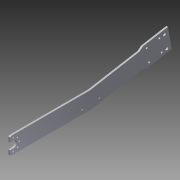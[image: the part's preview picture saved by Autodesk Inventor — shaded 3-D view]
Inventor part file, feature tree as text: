
AUTODESK INVENTOR PART (.ipt)
format: ipt  version: 2013 (Build 170138000, 138)  size: 186,368 bytes
history: native  units: mm
features: sketch x6, hole x5, other x2, extrude x2, pattern_circular x1
ambient origin geometry x8: Origin, YZ Plane, XZ Plane, XY Plane, X Axis, Y Axis, Z Axis, Center Point
feature tree (16):
  other  "ソリッド1"
  extrude  "押し出し1"  Depth=20.0mm
  hole  "穴2"  [1 undecoded]
  extrude  "押し出し2"  Depth=10.0mm
  hole  "穴3"  [1 undecoded]
  hole  "穴4"  [1 undecoded]
  pattern_circular  "円形状パターン3"  [2 undecoded]
  hole  "穴5"  [1 undecoded]
  hole  "穴6"  [1 undecoded]
  sketch  "スケッチ4"
  sketch  "スケッチ5"
  sketch  "スケッチ6"
  sketch  "スケッチ7"
  sketch  "スケッチ8"
  sketch  "スケッチ11"
  other  "断面エッジを投影1"
note: 7 required parameter values undecoded (feature->parameter linkage not recoverable at this tier; creation-order binding heuristic only, values carry confidence <= 0.55)
